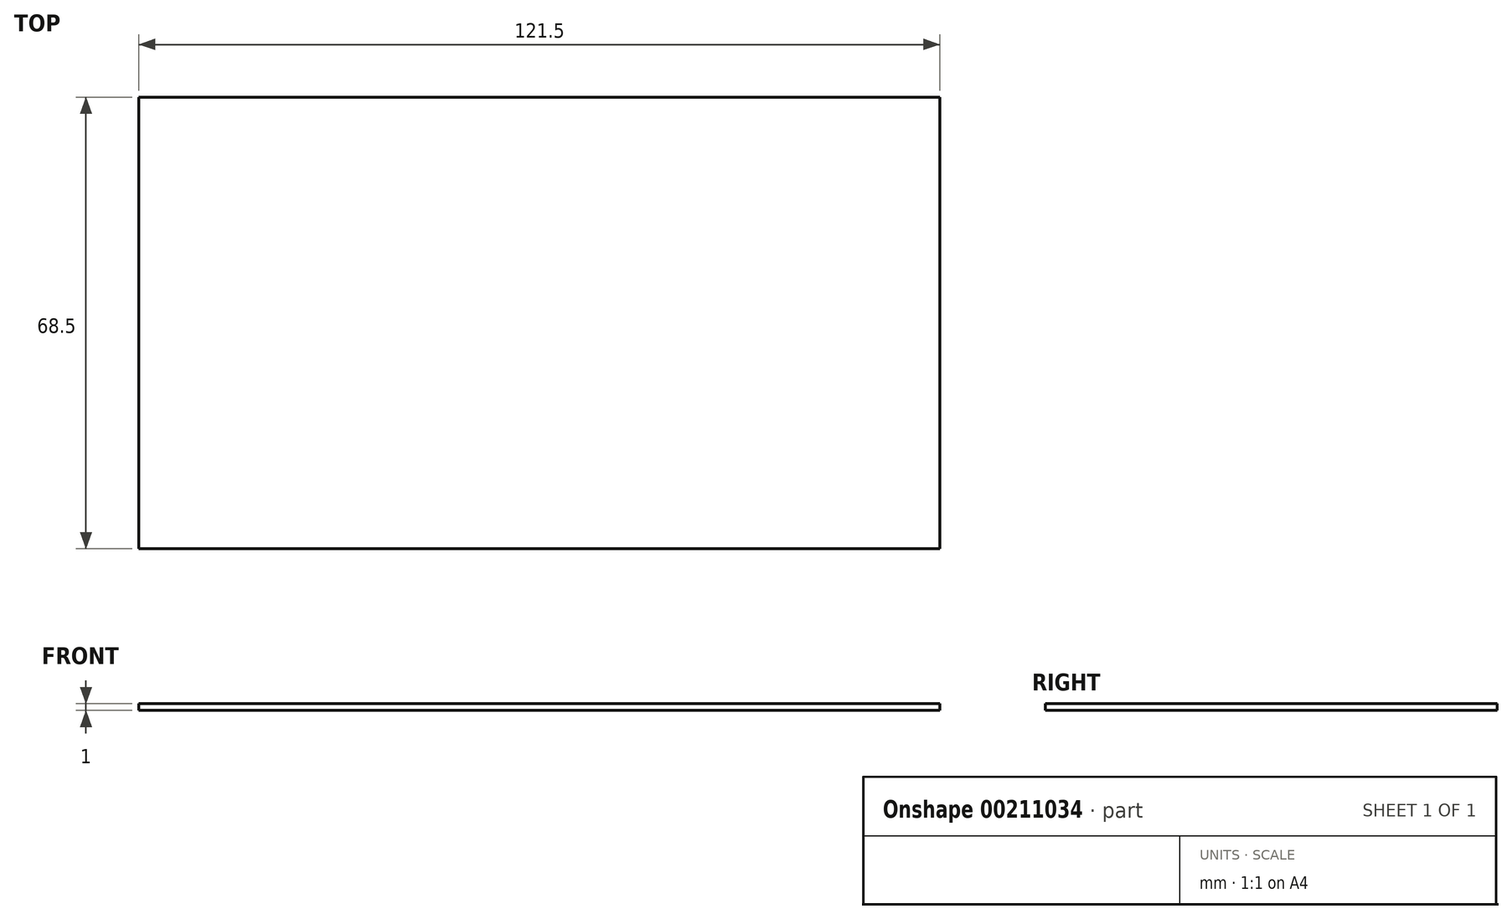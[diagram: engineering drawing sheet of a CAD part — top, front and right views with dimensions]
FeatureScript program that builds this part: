
annotation { "Feature Type Name" : "Feature", "Feature Type Description" : "" }
export const myFeature = defineFeature(function(context is Context, id is Id, definition is map)
    precondition{}
    {
        {
            var Q0;
            Q0=qCreatedBy(makeId("Top.planeOp"),FACE);
            var sketch = newSketch(context, id + "F0", { "sketchPlane" : qUnion([Q0])});
            skLineSegment(sketch, "E0.bottom", {"start": v(-60.75, -34.25) * mm, "end": v(60.75, -34.25) * mm});
            skLineSegment(sketch, "E0.top", {"start": v(-60.75, 34.25) * mm, "end": v(60.75, 34.25) * mm});
            skLineSegment(sketch, "E0.left", {"start": v(-60.75, -34.25) * mm, "end": v(-60.75, 34.25) * mm});
            skLineSegment(sketch, "E0.right", {"start": v(60.75, -34.25) * mm, "end": v(60.75, 34.25) * mm});
            skPoint(sketch, "E0.middle", {"position": v(0, 0) * mm});
            skSolve(sketch);
        }
        {
            var Q0;
            Q0=makeQuery(id+"F0.imprint","IMPRINT",FACE,{"disambiguationData":[TD([[makeQuery(id+"F0.imprint","IMPRINT",EDGE,{"derivedFrom":sQuery(id+"F0.wireOp",EDGE,"E0.bottom")}),1.0]])]});
            extrude(context, id + "F1", {"entities" : qUnion([Q0]), "depth" : 1 * mm});
        }
    });
